# Revit family: CADS_AIRFLOWdev_AirTerminal_UniversalRoofTerminal_Intake
name_source: partatom
category: Air Terminals
revit_build: Autodesk Revit 2015 (Build: 20160512_0715(x64)
units: mm (PartAtom-declared; Revit-internal decimal feet)

## types (3) — shared parameters
6MonthlyMaintenance = Visually inspect system, clean the fan and ducting if necessary
AirflowRateRange = 0-61
AssetType = Fixed
CEApproval = Yes
Default Elevation = 1219 mm
DurationUnit = Years
Exclusions = Incorrect Use / Incorrect Installation / Installed by a non-accredited electrician. Customer abuse.
FaceType = LOUVERED
FlowControlType = NONE
Grade = Virgin
GrossWeight = 1.53 kg
HasIntegralControl = No
HasSoundAttenuator = No
HasThermalInsulation = No
ISO140001 = Yes
ISO90001 = Yes
IsExtendedWarranty = No
Manufacturer = Airflow Developments Ltd
ManufacturerAddress = Aidelle House
Lancaster Road
Cressex Business Park
High Wycombe
Bucks
HP123QP
ManufacturerTelephone = 01494 525252
ManufacturerWebsite = www.airflow.com
Material = Plastic
MountingType = SURFACE
NBSCode = 90-75-50/370 Air terminals;
NominalHeight = 500 mm  [stored 1.64042 ft]
NominalLength = 215 mm
NominalWidth = 500 mm  [stored 1.64042 ft]
PointOfContact = Airflow Developments Ltd
ProductionYear = 2017
ReplacementCost = 157.26
ServiceLifeDuration = 10
ServiceLifeType = EXPECTEDSERVICELIFE
Shape = OTHER
ShippingWeight = 1.84 kg
Size = 215 x 500 x 500
Uniclass2015 = Pr_65_70_46_01
WarrantyContent = Replacement of part if faulty
WarrantyGuarantor = Airflow Developments Ltd
WarrantyPeriod = 2
zero-valued in all types: NumberOfSlots

## per-type parameters (varying)
| type | Description | GlobalTradeItemNumber | ModelLabel | ModelReference | Terminal |
| Anthracite | Universal Roof Terminal & Adaptor - Anthracite | 5019009313115 | Universal Roof Terminal & Adaptor - Anthracite | 90000349 | CADS_AirFlow_Anthracite |
| Sepia | Universal Roof Terminal & Adaptor - Sepia | 5019009313122 | Universal Roof Terminal & Adaptor - Sepia | 90000350 | CADS_AirFlow_Sepia |
| Terracotta | Universal Roof Terminal & Adaptor - Terracotta | 5019009313139 | Universal Roof Terminal & Adaptor - Terracotta | 90000351 | CADS_AirFlow_Terracotta |

note: column(s) folded — value = type name in every type: Color, Constituents

note: [stored X ft] marks values corroborated as IEEE doubles in the binary element streams (Revit-internal decimal feet)

## geometry (parser evidence)
native form markers: Blend x12, Sweep x2
no freeform markers — native parametric forms only
